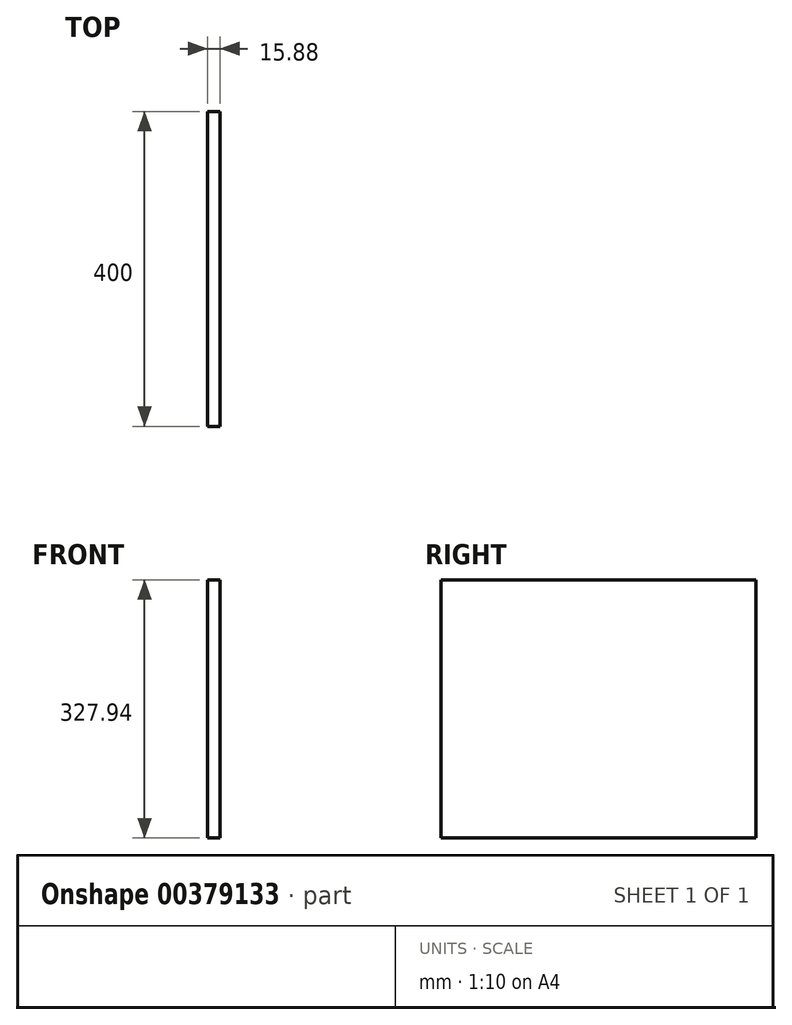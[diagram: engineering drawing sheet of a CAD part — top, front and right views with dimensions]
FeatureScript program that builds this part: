
annotation { "Feature Type Name" : "Feature", "Feature Type Description" : "" }
export const myFeature = defineFeature(function(context is Context, id is Id, definition is map)
    precondition{}
    {
        {
            var Q0;
            Q0=qCreatedBy(makeId("Front.planeOp"),FACE);
            var sketch = newSketch(context, id + "F0", { "sketchPlane" : qUnion([Q0])});
            skLineSegment(sketch, "E0.bottom", {"start": v(7.94, -163.97) * mm, "end": v(-7.94, -163.97) * mm});
            skLineSegment(sketch, "E0.top", {"start": v(7.94, 163.97) * mm, "end": v(-7.94, 163.97) * mm});
            skLineSegment(sketch, "E0.left", {"start": v(7.94, -163.97) * mm, "end": v(7.94, 163.97) * mm});
            skLineSegment(sketch, "E0.right", {"start": v(-7.94, -163.97) * mm, "end": v(-7.94, 163.97) * mm});
            skPoint(sketch, "E0.middle", {"position": v(0, 0) * mm});
            skSolve(sketch);
        }
        {
            var Q0;
            Q0=makeQuery(id+"F0.imprint","IMPRINT",FACE,{"disambiguationData":[TD([[makeQuery(id+"F0.imprint","IMPRINT",EDGE,{"derivedFrom":sQuery(id+"F0.wireOp",EDGE,"E0.bottom")}),-1.0]])]});
            extrude(context, id + "F1", {"entities" : qUnion([Q0]), "depth" : 400 * mm});
        }
    });
